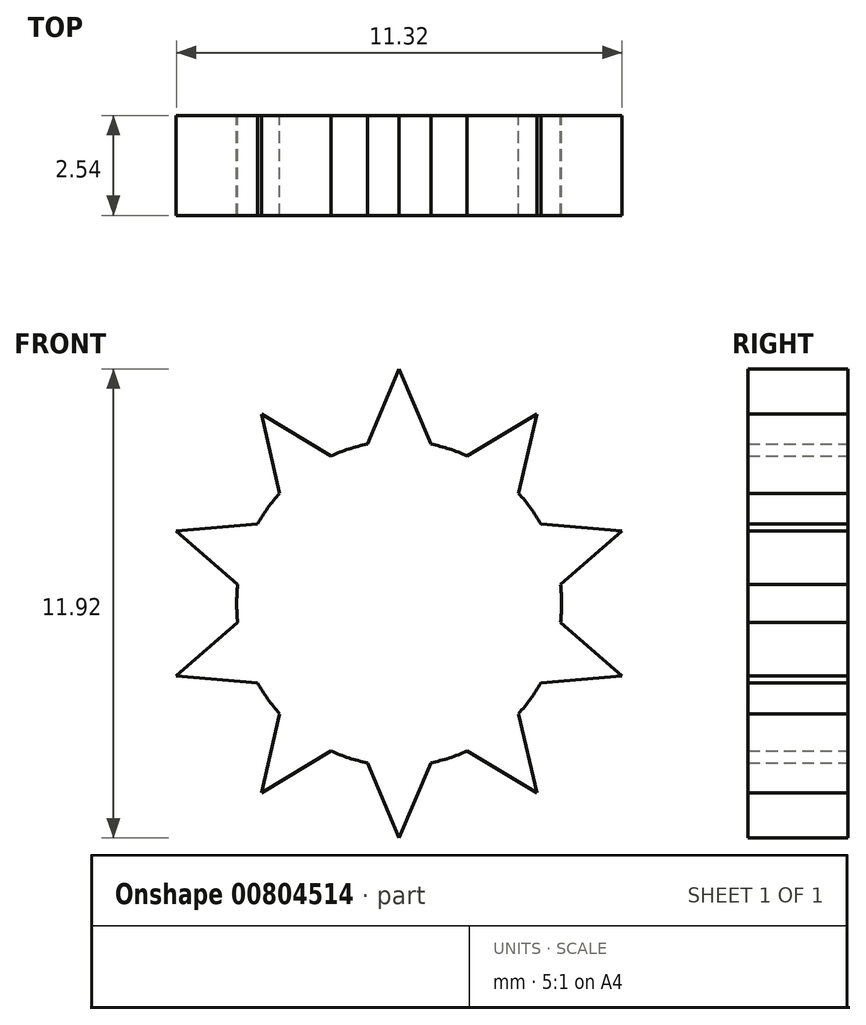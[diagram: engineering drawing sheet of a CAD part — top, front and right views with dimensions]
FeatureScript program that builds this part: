
annotation { "Feature Type Name" : "Feature", "Feature Type Description" : "" }
export const myFeature = defineFeature(function(context is Context, id is Id, definition is map)
    precondition{}
    {
        {
            var Q0;
            Q0=qCreatedBy(makeId("Front.planeOp"),FACE);
            var sketch = newSketch(context, id + "F0", { "sketchPlane" : qUnion([Q0])});
            skLineSegment(sketch, "E0.bottom", {"start": v(0, 0) * mm, "end": v(12.7, 0) * mm, "construction": true});
            skLineSegment(sketch, "E0.top", {"start": v(0, 12.7) * mm, "end": v(12.7, 12.7) * mm, "construction": true});
            skLineSegment(sketch, "E0.left", {"start": v(0, 0) * mm, "end": v(0, 12.7) * mm, "construction": true});
            skLineSegment(sketch, "E0.right", {"start": v(12.7, 0) * mm, "end": v(12.7, 12.7) * mm, "construction": true});
            skLineSegment(sketch, "E1", {"start": v(0, 6.35) * mm, "end": v(12.7, 6.35) * mm, "construction": true});
            skLineSegment(sketch, "E2", {"start": v(6.35, 12.7) * mm, "end": v(6.35, 0) * mm, "construction": true});
            skCircle(sketch, "E3", {"center": v(6.35, 6.35) * mm, "radius": 4.13 * mm, "construction": true});
            skCircle(sketch, "E4", {"center": v(6.35, 6.35) * mm, "radius": 4.13 * mm});
            skLineSegment(sketch, "E5", {"start": v(6.35, 10.48) * mm, "end": v(6.35, 12.3) * mm, "construction": true});
            skLineSegment(sketch, "E6", {"start": v(6.35, 12.3) * mm, "end": v(5.54, 10.4) * mm, "construction": true});
            skLineSegment(sketch, "E7", {"start": v(5.54, 10.4) * mm, "end": v(6.35, 12.3) * mm, "construction": true});
            skLineSegment(sketch, "E8", {"start": v(6.35, 12.3) * mm, "end": v(7.16, 10.4) * mm, "construction": true});
            skLineSegment(sketch, "E9", {"start": v(7.16, 10.4) * mm, "end": v(5.54, 10.4) * mm, "construction": true});
            skLineSegment(sketch, "E10", {"start": v(6.35, 12.3) * mm, "end": v(5.54, 10.4) * mm});
            skLineSegment(sketch, "E11", {"start": v(5.54, 10.4) * mm, "end": v(7.16, 10.4) * mm});
            skLineSegment(sketch, "E12", {"start": v(7.16, 10.4) * mm, "end": v(6.35, 12.3) * mm});
            skLineSegment(sketch, "E13.anchor1", {"start": v(6.35, 6.35) * mm, "end": v(5.54, 10.4) * mm, "construction": true});
            skLineSegment(sketch, "E13.anchor2", {"start": v(6.35, 6.35) * mm, "end": v(5.54, 10.4) * mm, "construction": true});
            skLineSegment(sketch, "E14.1.0", {"start": v(4.62, 10.1) * mm, "end": v(2.85, 11.17) * mm});
            skLineSegment(sketch, "E14.1.1", {"start": v(2.85, 11.17) * mm, "end": v(3.32, 9.15) * mm});
            skLineSegment(sketch, "E14.1.2", {"start": v(3.32, 9.15) * mm, "end": v(4.62, 10.1) * mm});
            skLineSegment(sketch, "E14.2.0", {"start": v(2.75, 8.37) * mm, "end": v(0.69, 8.2) * mm});
            skLineSegment(sketch, "E14.2.1", {"start": v(0.69, 8.2) * mm, "end": v(2.25, 6.83) * mm});
            skLineSegment(sketch, "E14.2.2", {"start": v(2.25, 6.83) * mm, "end": v(2.75, 8.37) * mm});
            skLineSegment(sketch, "E14.3.0", {"start": v(2.25, 5.87) * mm, "end": v(0.69, 4.5) * mm});
            skLineSegment(sketch, "E14.3.1", {"start": v(0.69, 4.5) * mm, "end": v(2.75, 4.33) * mm});
            skLineSegment(sketch, "E14.3.2", {"start": v(2.75, 4.33) * mm, "end": v(2.25, 5.87) * mm});
            skLineSegment(sketch, "E14.4.0", {"start": v(3.32, 3.55) * mm, "end": v(2.85, 1.53) * mm});
            skLineSegment(sketch, "E14.4.1", {"start": v(2.85, 1.53) * mm, "end": v(4.62, 2.6) * mm});
            skLineSegment(sketch, "E14.4.2", {"start": v(4.62, 2.6) * mm, "end": v(3.32, 3.55) * mm});
            skLineSegment(sketch, "E14.5.0", {"start": v(5.54, 2.3) * mm, "end": v(6.35, 0.4) * mm});
            skLineSegment(sketch, "E14.5.1", {"start": v(6.35, 0.4) * mm, "end": v(7.16, 2.3) * mm});
            skLineSegment(sketch, "E14.5.2", {"start": v(7.16, 2.3) * mm, "end": v(5.54, 2.3) * mm});
            skLineSegment(sketch, "E14.6.0", {"start": v(8.08, 2.6) * mm, "end": v(9.85, 1.53) * mm});
            skLineSegment(sketch, "E14.6.1", {"start": v(9.85, 1.53) * mm, "end": v(9.38, 3.55) * mm});
            skLineSegment(sketch, "E14.6.2", {"start": v(9.38, 3.55) * mm, "end": v(8.08, 2.6) * mm});
            skLineSegment(sketch, "E14.7.0", {"start": v(9.95, 4.33) * mm, "end": v(12.01, 4.5) * mm});
            skLineSegment(sketch, "E14.7.1", {"start": v(12.01, 4.5) * mm, "end": v(10.45, 5.87) * mm});
            skLineSegment(sketch, "E14.7.2", {"start": v(10.45, 5.87) * mm, "end": v(9.95, 4.33) * mm});
            skLineSegment(sketch, "E14.8.0", {"start": v(10.45, 6.83) * mm, "end": v(12.01, 8.2) * mm});
            skLineSegment(sketch, "E14.8.1", {"start": v(12.01, 8.2) * mm, "end": v(9.95, 8.37) * mm});
            skLineSegment(sketch, "E14.8.2", {"start": v(9.95, 8.37) * mm, "end": v(10.45, 6.83) * mm});
            skLineSegment(sketch, "E14.9.0", {"start": v(9.38, 9.15) * mm, "end": v(9.85, 11.17) * mm});
            skLineSegment(sketch, "E14.9.1", {"start": v(9.85, 11.17) * mm, "end": v(8.08, 10.1) * mm});
            skLineSegment(sketch, "E14.9.2", {"start": v(8.08, 10.1) * mm, "end": v(9.38, 9.15) * mm});
            skSolve(sketch);
        }
        {
            var Q0;
            Q0 = qSketchRegion(id + "F0", true);
            extrude(context, id + "F1", {"entities" : qUnion([Q0]), "depth" : 2.54 * mm, "offsetDistance" : 25.4 * mm});
        }
    });
